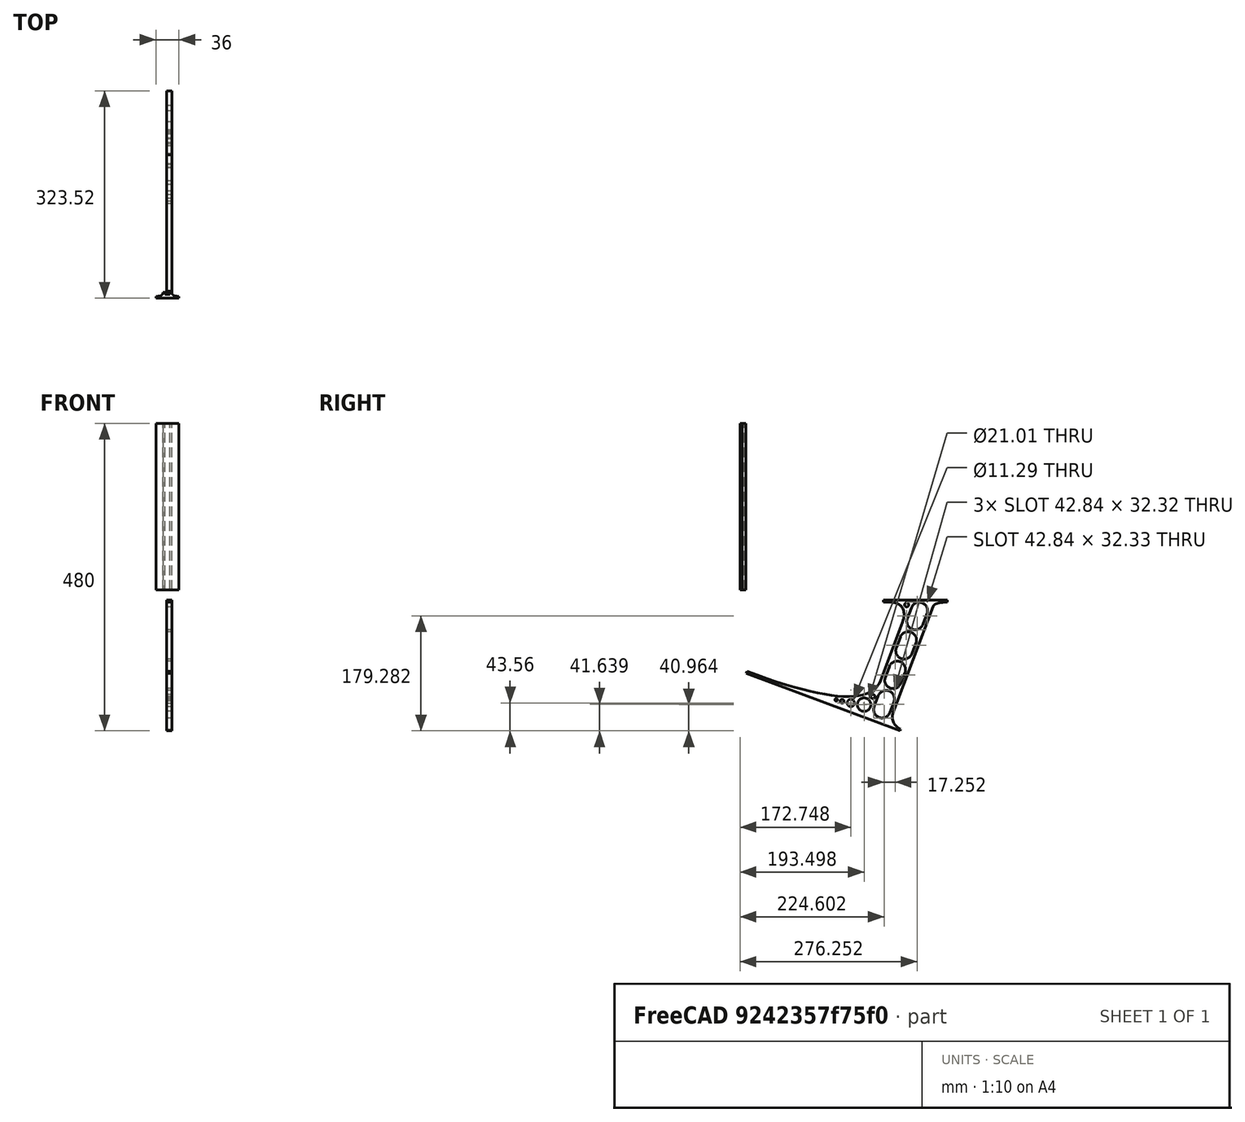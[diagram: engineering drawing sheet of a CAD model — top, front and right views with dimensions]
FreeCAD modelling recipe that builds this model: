
FCSTD DOCUMENT  (FreeCAD 0.19R0.19.2)
Label: laptopStand072
License: All rights reserved
LicenseURL: http://en.wikipedia.org/wiki/All_rights_reserved
objects: Sketcher::SketchObject×3, Part::Extrusion×3
note: 6 computed .brp shape members not serialized (recipe doc carries the construction recipe); baked Part::Feature solids carry a one-line shape summary decoded from their .brp

FEATURE [Sketcher::SketchObject] Sketch
  FullyConstrained = false
  sketch-geometry (152):
    g0: LineSegment StartX=-10.9272 StartY=-82.7794 StartZ=0 EndX=46.0728 EndY=-51.4823 EndZ=0
    g1: LineSegment StartX=366.073 StartY=-91.7794 StartZ=0 EndX=318.073 EndY=-65.424 EndZ=0
    g2: LineSegment StartX=-10.9272 StartY=77.3346 StartZ=0 EndX=-10.9272 EndY=-82.7794 EndZ=0
    g3: LineSegment StartX=375.073 StartY=-82.7794 StartZ=0 EndX=375.073 EndY=83.9235 EndZ=0
    g4: LineSegment StartX=-1.92719 StartY=-91.7794 StartZ=0 EndX=46.0728 EndY=-91.7794 EndZ=0
    g5: LineSegment StartX=318.073 StartY=124.221 StartZ=0 EndX=366.073 EndY=124.221 EndZ=0
    g6: LineSegment StartX=306.073 StartY=124.221 StartZ=0 EndX=189.124 EndY=27.0628 EndZ=0
    g7: LineSegment StartX=58.0728 StartY=-91.7794 StartZ=0 EndX=175.022 EndY=5.37834 EndZ=0
    g8: LineSegment StartX=58.0728 StartY=-81.8102 StartZ=0 EndX=58.0728 EndY=-58.8351 EndZ=0
    g9: LineSegment StartX=175.022 StartY=27.0628 StartZ=0 EndX=58.0728 EndY=124.221 EndZ=0
    g10: LineSegment StartX=189.124 StartY=5.37834 StartZ=0 EndX=306.073 EndY=-91.7794 EndZ=0
    g11: LineSegment StartX=306.073 StartY=77.3346 StartZ=0 EndX=306.073 EndY=-44.8935 EndZ=0
    g12: LineSegment StartX=318.073 StartY=83.9235 StartZ=0 EndX=318.073 EndY=-51.4823 EndZ=0
    g13: LineSegment StartX=306.073 StartY=-58.8351 StartZ=0 EndX=306.073 EndY=-81.8102 EndZ=0
    g14: LineSegment StartX=318.073 StartY=-51.4823 StartZ=0 EndX=375.073 EndY=-82.7794 EndZ=0
    g15: LineSegment StartX=318.073 StartY=-65.424 StartZ=0 EndX=318.073 EndY=-91.7794 EndZ=0
    g16: LineSegment StartX=318.073 StartY=-91.7794 StartZ=0 EndX=366.073 EndY=-91.7794 EndZ=0
    g17: LineSegment StartX=58.0728 StartY=-44.8935 StartZ=0 EndX=58.0728 EndY=77.3346 EndZ=0
    g18: LineSegment StartX=46.0728 StartY=-65.424 StartZ=0 EndX=-1.92719 EndY=-91.7794 EndZ=0
    g19: LineSegment StartX=46.0728 StartY=-65.424 StartZ=0 EndX=46.0728 EndY=-91.7794 EndZ=0
    g20: LineSegment StartX=58.0728 StartY=91.2763 StartZ=0 EndX=58.0728 EndY=114.251 EndZ=0
    g21: LineSegment StartX=46.0728 StartY=77.3346 StartZ=0 EndX=46.0728 EndY=-51.4823 EndZ=0
    g22: LineSegment StartX=-42.9272 StartY=136.221 StartZ=0 EndX=-42.9272 EndY=-103.779 EndZ=0
    g23: LineSegment StartX=407.073 StartY=136.221 StartZ=0 EndX=407.073 EndY=-103.779 EndZ=0
    g24: LineSegment StartX=179.022 StartY=27.0628 StartZ=0 EndX=179.022 EndY=124.221 EndZ=0
    g25: LineSegment StartX=185.124 StartY=27.0628 StartZ=0 EndX=185.124 EndY=124.221 EndZ=0
    g26: ArcOfCircle CenterX=-26.9272 CenterY=22.1087 CenterZ=0 NormalX=0 NormalY=0 NormalZ=1 AngleXU=0 Radius=8 StartAngle=1e-16 EndAngle=3.14159
    g27: ArcOfCircle CenterX=-26.9272 CenterY=-83.7794 CenterZ=0 NormalX=0 NormalY=0 NormalZ=1 AngleXU=0 Radius=8 StartAngle=3.14159 EndAngle=6.28319
    g28: LineSegment StartX=-34.9272 StartY=22.1087 StartZ=0 EndX=-34.9272 EndY=-83.7794 EndZ=0
    g29: LineSegment StartX=-18.9272 StartY=22.1087 StartZ=0 EndX=-18.9272 EndY=-83.7794 EndZ=0
    g30: LineSegment StartX=185.124 StartY=-91.7794 StartZ=0 EndX=306.073 EndY=-91.7794 EndZ=0
    g31: LineSegment StartX=179.022 StartY=-91.7794 StartZ=0 EndX=58.0728 EndY=-91.7794 EndZ=0
    g32: LineSegment StartX=306.073 StartY=124.221 StartZ=0 EndX=185.124 EndY=124.221 EndZ=0
    g33: LineSegment StartX=179.022 StartY=124.221 StartZ=0 EndX=58.0728 EndY=124.221 EndZ=0
    g34: ArcOfCircle CenterX=391.073 CenterY=22.1087 CenterZ=0 NormalX=0 NormalY=0 NormalZ=1 AngleXU=0 Radius=8 StartAngle=-4.4e-15 EndAngle=3.14159
    g35: LineSegment StartX=399.073 StartY=22.1087 StartZ=0 EndX=399.073 EndY=-83.7794 EndZ=0
    g36: LineSegment StartX=383.073 StartY=22.1087 StartZ=0 EndX=383.073 EndY=-83.7794 EndZ=0
    g37: ArcOfCircle CenterX=391.073 CenterY=-83.7794 CenterZ=0 NormalX=0 NormalY=0 NormalZ=1 AngleXU=0 Radius=8 StartAngle=3.14159 EndAngle=6.28319
    g38: Circle CenterX=175.022 CenterY=27.0628 CenterZ=0 NormalX=0 NormalY=0 NormalZ=1 AngleXU=0 Radius=1
    g39: Circle CenterX=179.022 CenterY=24.8665 CenterZ=0 NormalX=0 NormalY=0 NormalZ=1 AngleXU=0 Radius=1
    g40: Circle CenterX=179.022 CenterY=27.0628 CenterZ=0 NormalX=0 NormalY=0 NormalZ=1 AngleXU=0 Radius=1
    g41: BSplineCurve PolesCount=3 KnotsCount=2 Degree=2 IsPeriodic=0
    g42: GeomPoint X=175.022 Y=27.0628 Z=0
    g43: GeomPoint X=179.022 Y=27.0628 Z=0
    g44: Circle CenterX=189.124 CenterY=27.0628 CenterZ=0 NormalX=0 NormalY=0 NormalZ=1 AngleXU=0 Radius=1
    g45: Circle CenterX=185.124 CenterY=24.8665 CenterZ=0 NormalX=0 NormalY=0 NormalZ=1 AngleXU=0 Radius=1
    g46: Circle CenterX=185.124 CenterY=27.0628 CenterZ=0 NormalX=0 NormalY=0 NormalZ=1 AngleXU=0 Radius=1
    g47: BSplineCurve PolesCount=3 KnotsCount=2 Degree=2 IsPeriodic=0
    g48: GeomPoint X=189.124 Y=27.0628 Z=0
    g49: GeomPoint X=185.124 Y=27.0628 Z=0
    g50: Circle CenterX=175.022 CenterY=5.37834 CenterZ=0 NormalX=0 NormalY=0 NormalZ=1 AngleXU=0 Radius=1
    g51: Circle CenterX=179.022 CenterY=7.57463 CenterZ=0 NormalX=0 NormalY=0 NormalZ=1 AngleXU=0 Radius=1
    g52: Circle CenterX=179.022 CenterY=5.34704 CenterZ=0 NormalX=0 NormalY=0 NormalZ=1 AngleXU=0 Radius=1
    g53: BSplineCurve PolesCount=3 KnotsCount=2 Degree=2 IsPeriodic=0
    g54: GeomPoint X=175.022 Y=5.37834 Z=0
    g55: GeomPoint X=179.022 Y=5.34704 Z=0
    g56: Circle CenterX=189.124 CenterY=5.37834 CenterZ=0 NormalX=0 NormalY=0 NormalZ=1 AngleXU=0 Radius=1
    g57: Circle CenterX=185.124 CenterY=7.57463 CenterZ=0 NormalX=0 NormalY=0 NormalZ=1 AngleXU=0 Radius=1
    g58: Circle CenterX=185.124 CenterY=5.34704 CenterZ=0 NormalX=0 NormalY=0 NormalZ=1 AngleXU=0 Radius=1
    g59: BSplineCurve PolesCount=3 KnotsCount=2 Degree=2 IsPeriodic=0
    g60: GeomPoint X=189.124 Y=5.37834 Z=0
    g61: GeomPoint X=185.124 Y=5.34704 Z=0
    g62: LineSegment StartX=179.022 StartY=5.34704 StartZ=0 EndX=179.022 EndY=-91.7794 EndZ=0
    g63: LineSegment StartX=185.124 StartY=-91.7794 StartZ=0 EndX=185.124 EndY=5.34704 EndZ=0
    g64: Circle CenterX=165.871 CenterY=18.1458 CenterZ=0 NormalX=0 NormalY=0 NormalZ=1 AngleXU=0 Radius=1
    g65: Circle CenterX=169.377 CenterY=16.2206 CenterZ=0 NormalX=0 NormalY=0 NormalZ=1 AngleXU=0 Radius=1
    g66: Circle CenterX=165.871 CenterY=14.2954 CenterZ=0 NormalX=0 NormalY=0 NormalZ=1 AngleXU=0 Radius=1
    g67: BSplineCurve PolesCount=3 KnotsCount=2 Degree=2 IsPeriodic=0
    g68: GeomPoint X=165.871 Y=18.1458 Z=0
    g69: GeomPoint X=165.871 Y=14.2954 Z=0
    g70: Circle CenterX=198.275 CenterY=18.1458 CenterZ=0 NormalX=0 NormalY=0 NormalZ=1 AngleXU=0 Radius=1
    g71: Circle CenterX=194.768 CenterY=16.2206 CenterZ=0 NormalX=0 NormalY=0 NormalZ=1 AngleXU=0 Radius=1
    g72: Circle CenterX=198.275 CenterY=14.2954 CenterZ=0 NormalX=0 NormalY=0 NormalZ=1 AngleXU=0 Radius=1
    g73: BSplineCurve PolesCount=3 KnotsCount=2 Degree=2 IsPeriodic=0
    g74: GeomPoint X=198.275 Y=18.1458 Z=0
    g75: GeomPoint X=198.275 Y=14.2954 Z=0
    g76: LineSegment StartX=165.871 StartY=18.1458 StartZ=0 EndX=58.0728 EndY=77.3346 EndZ=0
    g77: LineSegment StartX=58.0728 StartY=-44.8935 StartZ=0 EndX=165.871 EndY=14.2954 EndZ=0
    g78: LineSegment StartX=198.275 StartY=18.1458 StartZ=0 EndX=306.073 EndY=77.3346 EndZ=0
    g79: LineSegment StartX=198.275 StartY=14.2954 StartZ=0 EndX=306.073 EndY=-44.8935 EndZ=0
    g80: LineSegment StartX=407.073 StartY=-103.779 StartZ=0 EndX=-42.9272 EndY=-103.779 EndZ=0
    g81: LineSegment StartX=407.073 StartY=136.221 StartZ=0 EndX=-42.9272 EndY=136.221 EndZ=0
    g82: LineSegment StartX=46.0728 StartY=77.3346 StartZ=0 EndX=-10.9272 EndY=77.3346 EndZ=0
    g83: LineSegment StartX=46.0728 StartY=105.865 StartZ=0 EndX=31.5028 EndY=105.865 EndZ=0
    g84: LineSegment StartX=46.0728 StartY=124.221 StartZ=0 EndX=46.0728 EndY=105.865 EndZ=0
    g85: LineSegment StartX=-1.92719 StartY=124.221 StartZ=0 EndX=31.5028 EndY=105.865 EndZ=0
    g86: LineSegment StartX=46.0728 StartY=124.221 StartZ=0 EndX=-1.92719 EndY=124.221 EndZ=0
    g87: LineSegment StartX=318.073 StartY=83.9235 StartZ=0 EndX=375.073 EndY=83.9235 EndZ=0
    g88: LineSegment StartX=318.073 StartY=105.865 StartZ=0 EndX=332.643 EndY=105.865 EndZ=0
    g89: LineSegment StartX=332.643 StartY=105.865 StartZ=0 EndX=366.073 EndY=124.221 EndZ=0
    g90: LineSegment StartX=318.073 StartY=124.221 StartZ=0 EndX=318.073 EndY=105.865 EndZ=0
    g91: Circle CenterX=125.607 CenterY=54.1951 CenterZ=0 NormalX=0 NormalY=0 NormalZ=1 AngleXU=0 Radius=1
    g92: Circle CenterX=139.632 CenterY=46.4944 CenterZ=0 NormalX=0 NormalY=0 NormalZ=1 AngleXU=0 Radius=1
    g93: Circle CenterX=127.326 CenterY=56.7187 CenterZ=0 NormalX=0 NormalY=0 NormalZ=1 AngleXU=0 Radius=1
    g94: BSplineCurve PolesCount=3 KnotsCount=2 Degree=2 IsPeriodic=0
    g95: GeomPoint X=125.607 Y=54.1951 Z=0
    g96: GeomPoint X=127.326 Y=56.7187 Z=0
    g97: LineSegment StartX=127.326 StartY=56.7187 StartZ=0 EndX=58.0728 EndY=114.251 EndZ=0
    g98: LineSegment StartX=58.0728 StartY=91.2763 StartZ=0 EndX=125.607 EndY=54.1951 EndZ=0
    g99: Circle CenterX=236.821 CenterY=56.7187 CenterZ=0 NormalX=0 NormalY=0 NormalZ=1 AngleXU=0 Radius=1
    g100: Circle CenterX=224.513 CenterY=46.4944 CenterZ=0 NormalX=0 NormalY=0 NormalZ=1 AngleXU=0 Radius=1
    g101: Circle CenterX=238.538 CenterY=54.1951 CenterZ=0 NormalX=0 NormalY=0 NormalZ=1 AngleXU=0 Radius=1
    g102: BSplineCurve PolesCount=3 KnotsCount=2 Degree=2 IsPeriodic=0
    g103: GeomPoint X=236.821 Y=56.7187 Z=0
    g104: GeomPoint X=238.538 Y=54.1951 Z=0
    g105: Circle CenterX=238.538 CenterY=-21.7539 CenterZ=0 NormalX=0 NormalY=0 NormalZ=1 AngleXU=0 Radius=1
    g106: Circle CenterX=224.513 CenterY=-14.0532 CenterZ=0 NormalX=0 NormalY=0 NormalZ=1 AngleXU=0 Radius=1
    g107: Circle CenterX=236.821 CenterY=-24.2775 CenterZ=0 NormalX=0 NormalY=0 NormalZ=1 AngleXU=0 Radius=1
    g108: BSplineCurve PolesCount=3 KnotsCount=2 Degree=2 IsPeriodic=0
    g109: GeomPoint X=238.538 Y=-21.7539 Z=0
    g110: GeomPoint X=236.821 Y=-24.2775 Z=0
    g111: LineSegment StartX=238.538 StartY=-21.7539 StartZ=0 EndX=306.073 EndY=-58.8351 EndZ=0
    g112: LineSegment StartX=236.821 StartY=-24.2775 StartZ=0 EndX=306.073 EndY=-81.8102 EndZ=0
    g113: Circle CenterX=125.607 CenterY=-21.7539 CenterZ=0 NormalX=0 NormalY=0 NormalZ=1 AngleXU=0 Radius=1
    g114: Circle CenterX=139.632 CenterY=-14.0532 CenterZ=0 NormalX=0 NormalY=0 NormalZ=1 AngleXU=0 Radius=1
    g115: Circle CenterX=127.325 CenterY=-24.2775 CenterZ=0 NormalX=0 NormalY=0 NormalZ=1 AngleXU=0 Radius=1
    g116: BSplineCurve PolesCount=3 KnotsCount=2 Degree=2 IsPeriodic=0
    g117: GeomPoint X=125.607 Y=-21.7539 Z=0
    g118: GeomPoint X=127.325 Y=-24.2775 Z=0
    g119: LineSegment StartX=125.607 StartY=-21.7539 StartZ=0 EndX=58.0728 EndY=-58.8351 EndZ=0
    g120: LineSegment StartX=127.325 StartY=-24.2775 StartZ=0 EndX=58.0728 EndY=-81.8102 EndZ=0
    g121: Circle CenterX=302.996 CenterY=111.695 CenterZ=0 NormalX=0 NormalY=0 NormalZ=1 AngleXU=0 Radius=1
    g122: Circle CenterX=306.073 CenterY=114.251 CenterZ=0 NormalX=0 NormalY=0 NormalZ=1 AngleXU=0 Radius=1
    g123: Circle CenterX=306.073 CenterY=110.251 CenterZ=0 NormalX=0 NormalY=0 NormalZ=1 AngleXU=0 Radius=1
    g124: BSplineCurve PolesCount=3 KnotsCount=2 Degree=2 IsPeriodic=0
    g125: GeomPoint X=302.996 Y=111.695 Z=0
    g126: GeomPoint X=306.073 Y=110.251 Z=0
    g127: Circle CenterX=306.073 CenterY=95.2763 CenterZ=0 NormalX=0 NormalY=0 NormalZ=1 AngleXU=0 Radius=1
    g128: Circle CenterX=306.073 CenterY=91.2763 CenterZ=0 NormalX=0 NormalY=0 NormalZ=1 AngleXU=0 Radius=1
    g129: Circle CenterX=302.567 CenterY=89.3511 CenterZ=0 NormalX=0 NormalY=0 NormalZ=1 AngleXU=0 Radius=1
    g130: BSplineCurve PolesCount=3 KnotsCount=2 Degree=2 IsPeriodic=0
    g131: GeomPoint X=306.073 Y=95.2763 Z=0
    g132: GeomPoint X=302.567 Y=89.3511 Z=0
    g133: LineSegment StartX=306.073 StartY=110.251 StartZ=0 EndX=306.073 EndY=95.2763 EndZ=0
    g134: LineSegment StartX=302.996 StartY=111.695 StartZ=0 EndX=236.821 EndY=56.7187 EndZ=0
    g135: LineSegment StartX=238.538 StartY=54.1951 StartZ=0 EndX=302.567 EndY=89.3511 EndZ=0
    g136: LineSegment StartX=58.0728 StartY=114.251 StartZ=0 EndX=61.1496 EndY=111.695 EndZ=0
    g137: LineSegment StartX=58.0728 StartY=114.251 StartZ=0 EndX=58.0728 EndY=110.251 EndZ=0
    g138: LineSegment StartX=58.0728 StartY=91.2763 StartZ=0 EndX=58.0728 EndY=95.2763 EndZ=0
    g139: LineSegment StartX=58.0728 StartY=91.2763 StartZ=0 EndX=61.5791 EndY=89.3511 EndZ=0
    g140: Circle CenterX=61.1496 CenterY=111.695 CenterZ=0 NormalX=0 NormalY=0 NormalZ=1 AngleXU=0 Radius=1
    g141: Circle CenterX=58.0728 CenterY=114.251 CenterZ=0 NormalX=0 NormalY=0 NormalZ=1 AngleXU=0 Radius=1
    g142: Circle CenterX=58.0728 CenterY=110.251 CenterZ=0 NormalX=0 NormalY=0 NormalZ=1 AngleXU=0 Radius=1
    g143: BSplineCurve PolesCount=3 KnotsCount=2 Degree=2 IsPeriodic=0
    g144: GeomPoint X=61.1496 Y=111.695 Z=0
    g145: GeomPoint X=58.0728 Y=110.251 Z=0
    g146: Circle CenterX=61.5791 CenterY=89.3511 CenterZ=0 NormalX=0 NormalY=0 NormalZ=1 AngleXU=0 Radius=1
    g147: Circle CenterX=58.0728 CenterY=91.2763 CenterZ=0 NormalX=0 NormalY=0 NormalZ=1 AngleXU=0 Radius=1
    g148: Circle CenterX=58.0728 CenterY=95.2763 CenterZ=0 NormalX=0 NormalY=0 NormalZ=1 AngleXU=0 Radius=1
    g149: BSplineCurve PolesCount=3 KnotsCount=2 Degree=2 IsPeriodic=0
    g150: GeomPoint X=61.5791 Y=89.3511 Z=0
    g151: GeomPoint X=58.0728 Y=95.2763 Z=0
  constraints (277):
    c: Horizontal(g4)
    c: Horizontal(g5)
    c: Tangent(g11,g13)
    c: Coincident(g12,g14)
    c: Coincident(g15,g1)
    c: Tangent(g12,g15)
    c: Tangent(g8,g17)
    c: Coincident(g19,g18)
    c: Coincident(g0,g21)
    c: Tangent(g17,g20)
    c: Block(g9)
    c: Block(g6)
    c: Block(g14)
    c: Block(g3)
    c: Block(g13)
    c: Block(g1)
    c: Block(g15)
    c: Block(g10)
    c: Block(g7)
    c: Block(g19)
    c: Block(g18)
    c: Block(g0)
    c: Block(g2)
    c: Block(g20)
    c: Block(g11)
    c: Block(g5)
    c: Block(g16)
    c: Block(g4)
    c: Vertical(g22)
    c: Vertical(g23)
    c: Block(g23)
    c: Block(g22)
    c: Vertical(g24)
    c: Vertical(g25)
    c: Block(g24)
    c: Block(g25)
    c: Tangent(g26,g29) = 1.5708
    c: Tangent(g26,g28) = -1.5708
    c: Tangent(g28,g27) = -1.5708
    c: Tangent(g29,g27) = 1.5708
    c: Vertical(g28)
    c: Equal(g26,g27)
    c: Block(g29)
    c: Block(g28)
    c: Coincident(g30,g10)
    c: Horizontal(g30)
    c: Coincident(g31,g7)
    c: Horizontal(g31)
    c: Coincident(g32,g6)
    c: Coincident(g32,g25)
    c: Horizontal(g32)
    c: Coincident(g33,g24)
    c: Coincident(g33,g9)
    c: Horizontal(g33)
    c: Tangent(g34,g35) = 1.5708
    c: Tangent(g35,g37) = 1.5708
    c: Equal(g34,g37)
    c: Coincident(g36,g34)
    c: Coincident(g36,g37)
    c: Block(g35)
    c: Block(g36)
    c: Coincident(g41,g9)
    c: Weight(g38) = 1
    c: Equal(g38,g39)
    c: Equal(g38,g40)
    c: Coincident(g41,g24)
    c: InternalAlignment(g38,g41)
    c: InternalAlignment(g39,g41)
    c: InternalAlignment(g40,g41)
    c: InternalAlignment(g42,g41)
    c: InternalAlignment(g43,g41)
    c: Coincident(g47,g6)
    c: Weight(g44) = 1
    c: Equal(g44,g45)
    c: Equal(g44,g46)
    c: Coincident(g47,g25)
    c: InternalAlignment(g44,g47)
    c: InternalAlignment(g45,g47)
    c: InternalAlignment(g46,g47)
    c: InternalAlignment(g48,g47)
    c: InternalAlignment(g49,g47)
    c: Block(g47)
    c: Block(g41)
    c: Coincident(g53,g7)
    c: Weight(g50) = 1
    c: Equal(g50,g51)
    c: Equal(g50,g52)
    c: InternalAlignment(g50,g53)
    c: InternalAlignment(g51,g53)
    c: InternalAlignment(g52,g53)
    c: InternalAlignment(g54,g53)
    c: InternalAlignment(g55,g53)
    c: Weight(g56) = 1
    c: Equal(g56,g57)
    c: Equal(g56,g58)
    c: InternalAlignment(g56,g59)
    c: InternalAlignment(g57,g59)
    c: InternalAlignment(g58,g59)
    c: InternalAlignment(g60,g59)
    c: InternalAlignment(g61,g59)
    c: Block(g59)
    c: Block(g53)
    c: Coincident(g62,g53)
    c: Coincident(g62,g31)
    c: Vertical(g62)
    c: Coincident(g63,g30)
    c: Coincident(g63,g59)
    c: Vertical(g63)
    c: Weight(g64) = 1
    c: Equal(g64,g65)
    c: Equal(g64,g66)
    c: InternalAlignment(g64,g67)
    c: InternalAlignment(g65,g67)
    c: InternalAlignment(g66,g67)
    c: InternalAlignment(g68,g67)
    c: InternalAlignment(g69,g67)
    c: Weight(g70) = 1
    c: Equal(g70,g71)
    c: Equal(g70,g72)
    c: InternalAlignment(g70,g73)
    c: InternalAlignment(g71,g73)
    c: InternalAlignment(g72,g73)
    c: InternalAlignment(g74,g73)
    c: InternalAlignment(g75,g73)
    c: Block(g67)
    c: Block(g73)
    c: Coincident(g76,g67)
    c: Coincident(g76,g17)
    c: Coincident(g77,g17)
    c: Coincident(g77,g67)
    c: Coincident(g78,g73)
    c: Coincident(g78,g11)
    c: Coincident(g79,g73)
    c: Coincident(g79,g11)
    c: Block(g17)
    c: Coincident(g80,g23)
    c: Coincident(g80,g22)
    c: Horizontal(g80)
    c: Distance(g80) = 450
    c: Coincident(g81,g23)
    c: Coincident(g81,g22)
    c: Horizontal(g81)
    c: Horizontal(g82)
    c: Coincident(g21,g82)
    c: Horizontal(g83)
    c: Vertical(g84)
    c: Block(g84)
    c: Block(g83)
    c: Block(g82)
    c: Distance(g84) = 18.3554
    c: Coincident(g86,g84)
    c: Coincident(g86,g85)
    c: Horizontal(g86)
    c: Block(g86)
    c: Block(g85)
    c: Coincident(g83,g85)
    c: Coincident(g2,g82)
    c: Coincident(g87,g12)
    c: Horizontal(g87)
    c: Horizontal(g88)
    c: Block(g87)
    c: Coincident(g89,g5)
    c: Coincident(g90,g5)
    c: Coincident(g90,g88)
    c: Vertical(g90)
    c: Block(g90)
    c: Coincident(g88,g89)
    c: Block(g89)
    c: Coincident(g3,g87)
    c: Weight(g91) = 1
    c: Equal(g91,g92)
    c: Equal(g91,g93)
    c: InternalAlignment(g91,g94)
    c: InternalAlignment(g92,g94)
    c: InternalAlignment(g93,g94)
    c: InternalAlignment(g95,g94)
    c: InternalAlignment(g96,g94)
    c: Block(g94)
    c: Coincident(g97,g94)
    c: Coincident(g97,g20)
    c: Coincident(g98,g20)
    c: Coincident(g98,g94)
    c: Weight(g99) = 1
    c: Equal(g99,g100)
    c: Equal(g99,g101)
    c: InternalAlignment(g99,g102)
    c: InternalAlignment(g100,g102)
    c: InternalAlignment(g101,g102)
    c: InternalAlignment(g103,g102)
    c: InternalAlignment(g104,g102)
    c: Block(g102)
    c: Weight(g105) = 1
    c: Equal(g105,g106)
    c: Equal(g105,g107)
    c: InternalAlignment(g105,g108)
    c: InternalAlignment(g106,g108)
    c: InternalAlignment(g107,g108)
    c: InternalAlignment(g109,g108)
    c: InternalAlignment(g110,g108)
    c: Block(g108)
    c: Coincident(g111,g108)
    c: Coincident(g111,g13)
    c: Coincident(g112,g108)
    c: Coincident(g112,g13)
    c: Weight(g113) = 1
    c: Equal(g113,g114)
    c: Equal(g113,g115)
    c: InternalAlignment(g113,g116)
    c: InternalAlignment(g114,g116)
    c: InternalAlignment(g115,g116)
    c: InternalAlignment(g117,g116)
    c: InternalAlignment(g118,g116)
    c: Block(g116)
    c: Coincident(g119,g116)
    c: Coincident(g119,g8)
    c: Coincident(g120,g116)
    c: Coincident(g120,g8)
    c: Block(g8)
    c: Weight(g121) = 1
    c: Equal(g121,g122)
    c: Equal(g121,g123)
    c: InternalAlignment(g121,g124)
    c: InternalAlignment(g122,g124)
    c: InternalAlignment(g123,g124)
    c: InternalAlignment(g125,g124)
    c: InternalAlignment(g126,g124)
    c: Weight(g127) = 1
    c: Equal(g127,g128)
    c: Equal(g127,g129)
    c: InternalAlignment(g127,g130)
    c: InternalAlignment(g128,g130)
    c: InternalAlignment(g129,g130)
    c: InternalAlignment(g131,g130)
    c: InternalAlignment(g132,g130)
    c: Block(g124)
    c: Block(g130)
    c: Coincident(g133,g124)
    c: Coincident(g133,g130)
    c: Vertical(g133)
    c: Coincident(g134,g124)
    c: Coincident(g134,g102)
    c: Coincident(g135,g102)
    c: Coincident(g135,g130)
    c: Vertical(g137)
    c: Parallel(g20,g138)
    c: Parallel(g136,g97)
    c: Parallel(g139,g98)
    c: Distance(g138) = 4
    c: Distance(g137) = 4
    c: Distance(g136) = 4
    c: Distance(g139) = 4
    c: Coincident(g139,g20)
    c: Coincident(g138,g20)
    c: Coincident(g137,g20)
    c: Coincident(g136,g20)
    c: Coincident(g143,g136)
    c: Weight(g140) = 1
    c: Equal(g140,g141)
    c: Coincident(g141,g20)
    c: Equal(g140,g142)
    c: Coincident(g143,g137)
    c: InternalAlignment(g140,g143)
    c: InternalAlignment(g141,g143)
    c: InternalAlignment(g142,g143)
    c: InternalAlignment(g144,g143)
    c: InternalAlignment(g145,g143)
    c: Coincident(g149,g139)
    c: Weight(g146) = 1
    c: Equal(g146,g147)
    c: Coincident(g147,g20)
    c: Equal(g146,g148)
    c: Coincident(g149,g138)
    c: InternalAlignment(g146,g149)
    c: InternalAlignment(g147,g149)
    c: InternalAlignment(g148,g149)
    c: InternalAlignment(g150,g149)
    c: InternalAlignment(g151,g149)
FEATURE [Sketcher::SketchObject] Sketch001
  FullyConstrained = true
  MapMode = 4
  Placement = pos=(0,0,0) rot=(0.57735,0.57735,0.57735;2.0944rad)
  Support = -> [Sketch]
  sketch-geometry (46):
    g0: BSplineCurve PolesCount=3 KnotsCount=2 Degree=2 IsPeriodic=0
    g1: ArcOfCircle CenterX=73.1223 CenterY=-32.291 CenterZ=0 NormalX=0 NormalY=0 NormalZ=1 AngleXU=0 Radius=13 StartAngle=5.92268 EndAngle=9.06428
    g2: ArcOfCircle CenterX=66.7816 CenterY=-49.1439 CenterZ=0 NormalX=0 NormalY=0 NormalZ=1 AngleXU=0 Radius=13 StartAngle=2.78068 EndAngle=5.92131
    g3: ArcOfCircle CenterX=55.9263 CenterY=-78.1807 CenterZ=0 NormalX=0 NormalY=0 NormalZ=1 AngleXU=0 Radius=13 StartAngle=5.92268 EndAngle=9.06428
    g4: ArcOfCircle CenterX=49.5884 CenterY=-95.0342 CenterZ=0 NormalX=0 NormalY=0 NormalZ=1 AngleXU=0 Radius=13 StartAngle=2.78068 EndAngle=5.92131
    g5: ArcOfCircle CenterX=38.7206 CenterY=-124.067 CenterZ=0 NormalX=0 NormalY=0 NormalZ=1 AngleXU=0 Radius=13 StartAngle=5.92268 EndAngle=9.06428
    g6: ArcOfCircle CenterX=32.3875 CenterY=-140.92 CenterZ=0 NormalX=0 NormalY=0 NormalZ=1 AngleXU=0 Radius=13 StartAngle=2.78068 EndAngle=5.92131
    g7: ArcOfCircle CenterX=21.4715 CenterY=-169.934 CenterZ=0 NormalX=0 NormalY=0 NormalZ=1 AngleXU=0 Radius=13 StartAngle=5.92268 EndAngle=9.06428
    g8: ArcOfCircle CenterX=15.1336 CenterY=-186.787 CenterZ=0 NormalX=0 NormalY=0 NormalZ=1 AngleXU=0 Radius=13 StartAngle=2.78068 EndAngle=5.92131
    g9-g12: Circle x4 (B-spline internal-alignment scaffolding for g13; pole/knot coordinates omitted)
    g13: BSplineCurve PolesCount=4 KnotsCount=2 Degree=3 IsPeriodic=0
    g14: GeomPoint X=28.8094 Y=-19.0875 Z=0
    g15: GeomPoint X=47.0443 Y=-50.4712 Z=0
    g16: Circle CenterX=53.5586 CenterY=-23.2695 CenterZ=0 NormalX=0 NormalY=0 NormalZ=1 AngleXU=0 Radius=3.24518
    g17: Circle CenterX=-195.441 CenterY=-127.082 CenterZ=0 NormalX=0 NormalY=0 NormalZ=1 AngleXU=0 Radius=1
    g18: Circle CenterX=-8.24091 CenterY=-197.481 CenterZ=0 NormalX=0 NormalY=0 NormalZ=1 AngleXU=0 Radius=1
    g19: Circle CenterX=12.8789 CenterY=-141.321 CenterZ=0 NormalX=0 NormalY=0 NormalZ=1 AngleXU=0 Radius=1
    g20: BSplineCurve PolesCount=3 KnotsCount=2 Degree=2 IsPeriodic=0
    g21: GeomPoint X=-195.441 Y=-127.082 Z=0
    g22: GeomPoint X=12.8789 Y=-141.321 Z=0
    g23: Circle CenterX=-12.8016 CenterY=-179.036 CenterZ=0 NormalX=0 NormalY=0 NormalZ=1 AngleXU=0 Radius=10.5072
    g24: Circle CenterX=0.933922 CenterY=-166.43 CenterZ=0 NormalX=0 NormalY=0 NormalZ=1 AngleXU=0 Radius=3.26661
    g25: Circle CenterX=-33.5518 CenterY=-176.44 CenterZ=0 NormalX=0 NormalY=0 NormalZ=1 AngleXU=0 Radius=5.64388
    g26: Circle CenterX=-47.2366 CenterY=-173.859 CenterZ=0 NormalX=0 NormalY=0 NormalZ=1 AngleXU=0 Radius=3.01653
    g27: Circle CenterX=-56.2595 CenterY=-171.456 CenterZ=0 NormalX=0 NormalY=0 NormalZ=1 AngleXU=0 Radius=2.12826
    g28: ArcOfCircle CenterX=51.2151 CenterY=-198.473 CenterZ=0 NormalX=0 NormalY=0 NormalZ=1 AngleXU=0 Radius=20 StartAngle=2.78189 EndAngle=4.35269
    g29: LineSegment StartX=32.4951 StartY=-191.433 StartZ=0 EndX=94.6578 EndY=-26.1352 EndZ=0
    g30: LineSegment StartX=43.1192 StartY=-220.001 StartZ=0 EndX=-196.497 EndY=-129.89 EndZ=0
    g31: LineSegment StartX=43.1192 StartY=-220.001 StartZ=0 EndX=44.1752 EndY=-217.193 EndZ=0
    g32: LineSegment StartX=117.223 StartY=-19.0875 StartZ=0 EndX=117.223 EndY=-16.0875 EndZ=0
    g33: LineSegment StartX=117.223 StartY=-16.0875 StartZ=0 EndX=17.2232 EndY=-16.0875 EndZ=0
    g34: LineSegment StartX=17.2232 StartY=-16.0875 StartZ=0 EndX=17.2232 EndY=-19.0875 EndZ=0
    g35: LineSegment StartX=28.8094 StartY=-19.0875 StartZ=0 EndX=17.2232 EndY=-19.0875 EndZ=0
    g36: LineSegment StartX=47.0443 StartY=-50.4712 StartZ=0 EndX=12.8789 EndY=-141.321 EndZ=0
    g37: LineSegment StartX=-195.441 StartY=-127.082 StartZ=0 EndX=-196.497 EndY=-129.89 EndZ=0
    g38: LineSegment StartX=85.2866 StartY=-36.8766 StartZ=0 EndX=78.9396 EndY=-53.7463 EndZ=0
    g39: LineSegment StartX=60.9579 StartY=-27.7053 StartZ=0 EndX=54.6191 EndY=-44.5532 EndZ=0
    g40: LineSegment StartX=68.0907 StartY=-82.7664 StartZ=0 EndX=61.7465 EndY=-99.6365 EndZ=0
    g41: LineSegment StartX=43.7619 StartY=-73.595 StartZ=0 EndX=37.426 EndY=-90.4435 EndZ=0
    g42: LineSegment StartX=50.885 StartY=-128.652 StartZ=0 EndX=44.5456 EndY=-145.522 EndZ=0
    g43: LineSegment StartX=26.5562 StartY=-119.481 StartZ=0 EndX=20.2251 EndY=-136.329 EndZ=0
    g44: LineSegment StartX=9.3071 StartY=-165.349 StartZ=0 EndX=2.97115 EndY=-182.197 EndZ=0
    g45: LineSegment StartX=33.6358 StartY=-174.52 StartZ=0 EndX=27.2917 EndY=-191.39 EndZ=0
  constraints (71):
    c: Block(g0)
    c: Block(g1)
    c: Block(g2)
    c: Block(g4)
    c: Block(g3)
    c: Block(g6)
    c: Block(g5)
    c: Block(g8)
    c: Block(g7)
    c: Weight(g9) = 1
    c: Equal(g9,g10)
    c: Equal(g9,g11)
    c: Equal(g9,g12)
    c: InternalAlignment(g9-g12 -> g13) x4
    c: InternalAlignment(g14,g13)
    c: InternalAlignment(g15,g13)
    c: Block(g16)
    c: Weight(g17) = 1
    c: Equal(g17,g18)
    c: Equal(g17,g19)
    c: InternalAlignment(g17,g20)
    c: InternalAlignment(g18,g20)
    c: InternalAlignment(g19,g20)
    c: InternalAlignment(g21,g20)
    c: InternalAlignment(g22,g20)
    c: Block(g20)
    c: Block(g23)
    c: Block(g24)
    c: Block(g25)
    c: Block(g26)
    c: Block(g27)
    c: Block(g28)
    c: Coincident(g29,g28)
    c: Coincident(g29,g0)
    c: Block(g13)
    c: Coincident(g31,g30)
    c: Coincident(g31,g28)
    c: Block(g31)
    c: Coincident(g32,g0)
    c: Vertical(g32)
    c: Coincident(g33,g32)
    c: Horizontal(g33)
    c: Coincident(g34,g33)
    c: Vertical(g34)
    c: Block(g33)
    c: Coincident(g35,g13)
    c: Coincident(g35,g34)
    c: Horizontal(g35)
    c: Coincident(g36,g13)
    c: Coincident(g36,g20)
    c: Coincident(g37,g20)
    c: Coincident(g37,g30)
    c: Block(g30)
    c: Coincident(g38,g1)
    c: Coincident(g38,g2)
    c: Coincident(g39,g1)
    c: Coincident(g39,g2)
    c: Coincident(g40,g3)
    c: Coincident(g40,g4)
    c: Coincident(g41,g3)
    c: Coincident(g41,g4)
    c: Coincident(g42,g5)
    c: Coincident(g42,g6)
    c: Coincident(g43,g5)
    c: Coincident(g43,g6)
    c: Coincident(g44,g7)
    c: Coincident(g44,g8)
    c: Coincident(g45,g7)
    c: Coincident(g45,g8)
    c: Distance(g30) = 256
    c: Distance(g33) = 100
FEATURE [Part::Extrusion] Extrude002
  Base = -> Sketch001
  Dir = (1,0,0)
  DirMode = 2
  FaceMakerClass = Part::FaceMakerBullseye
  LengthFwd = 8
  LengthRev = 0
  Solid = true
  Symmetric = false
FEATURE [Sketcher::SketchObject] Sketch002
  FullyConstrained = true
  sketch-geometry (20):
    g0: LineSegment StartX=-2.77179 StartY=-200.304 StartZ=0 EndX=5.22821 EndY=-200.304 EndZ=0
    g1: LineSegment StartX=5.22821 StartY=-200.304 StartZ=0 EndX=5.22821 EndY=-197.304 EndZ=0
    g2: LineSegment StartX=-2.77179 StartY=-200.304 StartZ=0 EndX=-2.77179 EndY=-197.304 EndZ=0
    g3: LineSegment StartX=5.22821 StartY=-197.304 StartZ=0 EndX=8.22821 EndY=-197.304 EndZ=0
    g4: LineSegment StartX=-2.77179 StartY=-197.304 StartZ=0 EndX=-5.77179 EndY=-197.304 EndZ=0
    g5: LineSegment StartX=19.2282 StartY=-203.304 StartZ=0 EndX=19.2282 EndY=-206.304 EndZ=0
    g6: LineSegment StartX=-16.7718 StartY=-203.304 StartZ=0 EndX=-16.7718 EndY=-206.304 EndZ=0
    g7: LineSegment StartX=-16.7718 StartY=-206.304 StartZ=0 EndX=19.2282 EndY=-206.304 EndZ=0
    g8: Circle CenterX=-16.7718 CenterY=-203.304 CenterZ=0 NormalX=0 NormalY=0 NormalZ=1 AngleXU=0 Radius=1
    g9: Circle CenterX=-5.77179 CenterY=-203.304 CenterZ=0 NormalX=0 NormalY=0 NormalZ=1 AngleXU=0 Radius=1
    g10: Circle CenterX=-5.77179 CenterY=-197.304 CenterZ=0 NormalX=0 NormalY=0 NormalZ=1 AngleXU=0 Radius=1
    g11: BSplineCurve PolesCount=3 KnotsCount=2 Degree=2 IsPeriodic=0
    g12: GeomPoint X=-16.7718 Y=-203.304 Z=0
    g13: GeomPoint X=-5.77179 Y=-197.304 Z=0
    g14: Circle CenterX=19.2282 CenterY=-203.304 CenterZ=0 NormalX=0 NormalY=0 NormalZ=1 AngleXU=0 Radius=1
    g15: Circle CenterX=8.22821 CenterY=-203.304 CenterZ=0 NormalX=0 NormalY=0 NormalZ=1 AngleXU=0 Radius=1
    g16: Circle CenterX=8.22821 CenterY=-197.304 CenterZ=0 NormalX=0 NormalY=0 NormalZ=1 AngleXU=0 Radius=1
    g17: BSplineCurve PolesCount=3 KnotsCount=2 Degree=2 IsPeriodic=0
    g18: GeomPoint X=19.2282 Y=-203.304 Z=0
    g19: GeomPoint X=8.22821 Y=-197.304 Z=0
  constraints (41):
    c: Horizontal(g0)
    c: Distance(g0) = 8
    c: Coincident(g1,g0)
    c: Vertical(g1)
    c: Distance(g1) = 3
    c: Coincident(g2,g0)
    c: Vertical(g2)
    c: Distance(g2) = 3
    c: Coincident(g3,g1)
    c: Horizontal(g3)
    c: Distance(g3) = 3
    c: Coincident(g4,g2)
    c: Horizontal(g4)
    c: Distance(g4) = 3
    c: Vertical(g5)
    c: Vertical(g6)
    c: Coincident(g7,g6)
    c: Coincident(g7,g5)
    c: Weight(g8) = 1
    c: Equal(g8,g9)
    c: Equal(g8,g10)
    c: Coincident(g11,g4)
    c: InternalAlignment(g8,g11)
    c: InternalAlignment(g9,g11)
    c: InternalAlignment(g10,g11)
    c: InternalAlignment(g12,g11)
    c: InternalAlignment(g13,g11)
    c: Coincident(g17,g5)
    c: Weight(g14) = 1
    c: Equal(g14,g15)
    c: Equal(g14,g16)
    c: Coincident(g17,g3)
    c: InternalAlignment(g14,g17)
    c: InternalAlignment(g15,g17)
    c: InternalAlignment(g16,g17)
    c: InternalAlignment(g18,g17)
    c: InternalAlignment(g19,g17)
    c: Block(g7)
    c: Block(g17)
    c: Block(g11)
    c: Block(g6)
FEATURE [Part::Extrusion] Extrude003
  Base = -> Sketch002
  Dir = (0,0,1)
  DirMode = 2
  FaceMakerClass = Part::FaceMakerBullseye
  LengthFwd = 260
  LengthRev = 0
  Solid = true
  Symmetric = false
FEATURE [Part::Extrusion] Extrude
  Base = -> Sketch
  Dir = (0,0,1)
  DirMode = 2
  FaceMakerClass = Part::FaceMakerBullseye
  LengthFwd = 14
  LengthRev = 0
  Solid = true
  Symmetric = false
